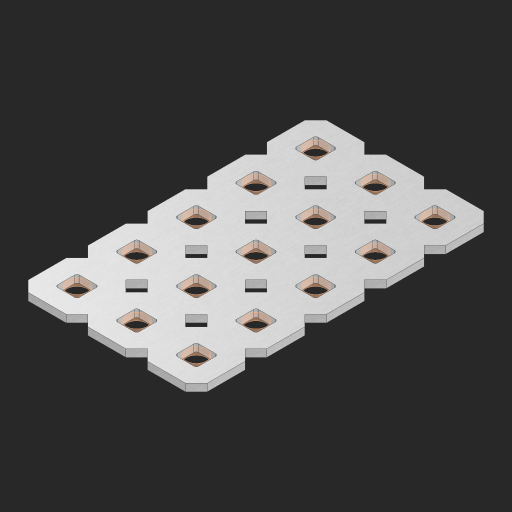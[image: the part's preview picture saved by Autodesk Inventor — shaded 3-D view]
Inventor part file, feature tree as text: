
AUTODESK INVENTOR PART (.ipt)
format: ipt  version: 2023 (Build 270158000, 158)  size: 471,552 bytes
history: native  units: in
note: dims shown in document units (in); Inventor stores cm internally (conversion verified against a paired STEP export)
features: other x16, extrude x14, sketch x2, pattern_linear x1
ambient origin geometry x8: Origin, YZ Plane, XZ Plane, XY Plane, X Axis, Y Axis, Z Axis, Center Point
bodies: Solid1 (feature_tree), Body (feature_tree)
feature tree (33):
  pattern_linear  "Rectangular Pattern1"  Spacing1=0.09in  [1 undecoded]
  sketch  "Sketch1"  dims[d1=0.5in]
  sketch  "Sketch2"  dims[d2=0.182in d3=0.09in d4=0.09in d5=0.09in d6=0.09in d7=0.09in d8=0.09in d9=0.09in d10=0.09in d11=0.02in d13=0.0in d14=0.172in d15=0.0625in d16=0.0in d19=0.5in d22=0.5in]
  other  "Srf1"
  other  "Srf126"
  other  "Srf127"
  other  "Srf128"
  other  "Srf129"
  other  "Srf268"
  other  "Srf269"
  other  "Srf270"
  other  "Srf271"
  other  "Srf272"
  other  "Srf293"
  other  "Srf294"
  other  "Srf295"
  other  "Srf296"
  other  "Srf297"
  other  "Circle"
  extrude  "ExtrusionSrf126"  Depth=0.09in
  extrude  "ExtrusionSrf127"  Depth=0.09in
  extrude  "ExtrusionSrf128"  Depth=0.09in
  extrude  "ExtrusionSrf129"  Depth=0.09in
  extrude  "ExtrusionSrf268"  Depth=0.09in
  extrude  "ExtrusionSrf269"  Depth=0.09in
  extrude  "ExtrusionSrf270"  Depth=0.09in
  extrude  "ExtrusionSrf271"  Depth=0.02in
  extrude  "ExtrusionSrf272"  TaperAngle=0.0deg  [1 undecoded]
  extrude  "ExtrusionSrf293"  Depth=0.5in
  extrude  "ExtrusionSrf294"  Depth=0.0625in TaperAngle=0.0deg
  extrude  "ExtrusionSrf295"  Depth=0.5in
  extrude  "ExtrusionSrf296"  Depth=0.5in
  extrude  "ExtrusionSrf297"  [1 undecoded]
note: 3 required parameter values undecoded (feature->parameter linkage not recoverable at this tier; creation-order binding heuristic only, values carry confidence <= 0.55)
